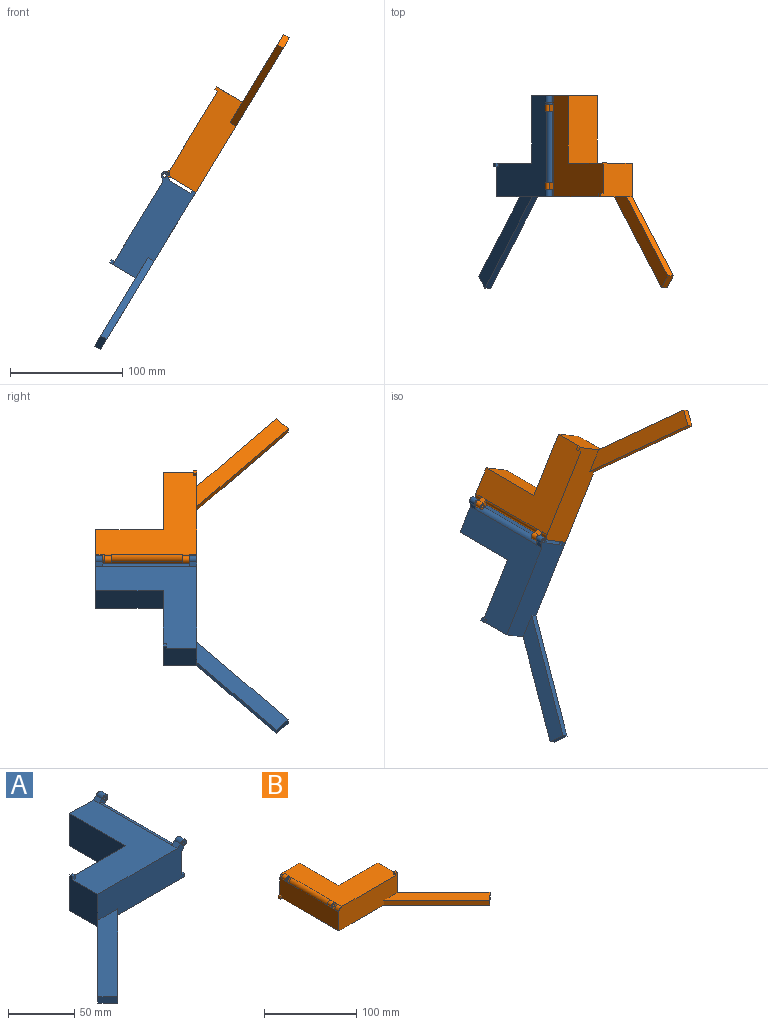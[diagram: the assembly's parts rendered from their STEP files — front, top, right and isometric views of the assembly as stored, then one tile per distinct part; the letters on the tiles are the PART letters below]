
ASSEMBLY  parts=2 mates=1
PART A: 29 faces, bbox 165.4x171.3x34.7 mm
  f0: plane 90x25.32mm, normal (1,0,0), area 2267mm2, adj f5,f9,f10,f13,f16,f17,f18,f21
  f1: plane 90x85.32mm, normal (0,0,1), area 4067mm2, adj f5,f6,f7,f8,f9,f13,f16,f19
  f2: plane 70.71x70.71mm, normal (-0.71,0.71,0), area 600mm2, adj f3,f8,f10,f22
  f3: plane 10.61x10.61mm, normal (-0.71,-0.71,0), area 90mm2, adj f2,f4,f10,f22
  f4: plane 81.32x81.32mm, normal (0.71,-0.71,0), area 690mm2, adj f3,f9,f10,f22
  f5: plane 34.68x34.68mm, normal (0,1,0), area 930.6mm2, adj f0,f1,f6,f10,f14,f15,f17,f20
  f6: plane 60x30mm, normal (-1,0,0), area 1800mm2, adj f1,f5,f7,f10
  f7: plane 60x32.96mm, normal (0,1,0), area 1809.2mm2, adj f1,f6,f8,f10,f24,f25
  f8: plane 32.96x30mm, normal (-1,0,0), area 909.2mm2, adj f1,f2,f7,f9,f10,f23,f25
  f9: plane 94.68x34.68mm, normal (0,-1,0), area 2612.5mm2, adj f0,f1,f4,f8,f10,f11,f12,f18
  f10: plane 171.32x163.67mm, normal (0,0,-1), area 6121.7mm2, adj f0,f2,f3,f4,f5,f6,f7,f8
  f11: cylinder r=3.12mm len=6.24mm, axis (0,-1,0), area 79.7mm2, adj f9,f13,f18,f19
  f12: cylinder r=1.56mm len=6.24mm, axis (0,-1,0), area 61.2mm2, adj f9,f13
  f13: plane 9.53x9.53mm, normal (0,1,0), area 35.3mm2, adj f0,f1,f11,f12,f18,f19,f21
  f14: cylinder r=3.12mm len=6.24mm, axis (0,1,0), area 79.7mm2, adj f5,f16,f17,f20
  f15: cylinder r=1.56mm len=6.24mm, axis (0,1,0), area 61.2mm2, adj f5,f16
  f16: plane 9.53x9.53mm, normal (0,-1,0), area 35.3mm2, adj f0,f1,f14,f15,f17,f20,f21
  f17: plane 6.24x3.43mm, normal (0.81,0,-0.59), area 26.5mm2, adj f0,f5,f14,f16
  f18: plane 6.24x3.43mm, normal (0.81,0,-0.59), area 26.5mm2, adj f0,f9,f11,f13
  f19: plane 6.24x3.43mm, normal (-0.59,0,0.81), area 26.5mm2, adj f1,f9,f11,f13
  f20: plane 6.24x3.43mm, normal (-0.59,0,0.81), area 26.5mm2, adj f1,f5,f14,f16
  f21: cylinder r=4.68mm len=77.52mm, axis (0,-1,0), area 569.9mm2, adj f0,f1,f13,f16
  f22: plane 91.92x81.32mm, normal (0,0,1), area 1612.5mm2, adj f2,f3,f4,f9
  f23: plane 3.12x2.96mm, normal (0,-1,0), area 9.2mm2, adj f1,f8,f24,f25
  f24: plane 3.12x2.96mm, normal (1,0,0), area 9.2mm2, adj f1,f7,f23,f25
  f25: plane 3.12x3.12mm, normal (0,0,1), area 9.7mm2, adj f7,f8,f23,f24
  f26: plane 3.12x2.96mm, normal (0,0,1), area 9.2mm2, adj f0,f9,f27,f28
  f27: plane 3.12x2.96mm, normal (0,1,0), area 9.2mm2, adj f0,f10,f26,f28
  f28: plane 3.12x3.12mm, normal (1,0,0), area 9.7mm2, adj f9,f10,f26,f27
PART B: 33 faces, bbox 165.4x171.3x34.7 mm
  f0: plane 90x25.32mm, normal (-1,0,0), area 2267mm2, adj f2,f9,f10,f13,f14,f17,f18,f19
  f1: plane 90x85.32mm, normal (0,0,1), area 4067mm2, adj f2,f3,f4,f5,f9,f13,f14,f17
  f2: plane 32.96x30mm, normal (0,1,0), area 904.5mm2, adj f0,f1,f3,f10,f25,f30,f32
  f3: plane 60x30mm, normal (1,0,0), area 1800mm2, adj f1,f2,f4,f10
  f4: plane 60x30mm, normal (0,1,0), area 1800mm2, adj f1,f3,f5,f10
  f5: plane 32.96x30mm, normal (1,0,0), area 909.2mm2, adj f1,f4,f6,f9,f10,f27,f29
  f6: plane 70.71x70.71mm, normal (0.71,0.71,0), area 600mm2, adj f5,f7,f10,f26
  f7: plane 10.61x10.61mm, normal (0.71,-0.71,0), area 90mm2, adj f6,f8,f10,f26
  f8: plane 81.32x81.32mm, normal (-0.71,-0.71,0), area 690mm2, adj f7,f9,f10,f26
  f9: plane 90x32.96mm, normal (0,-1,0), area 2577.3mm2, adj f0,f1,f5,f8,f10,f23,f26,f28
  f10: plane 171.32x163.67mm, normal (0,0,-1), area 6121.7mm2, adj f0,f2,f3,f4,f5,f6,f7,f8
  f11: cylinder r=1.56mm len=6.24mm, axis (0,1,0), area 61.2mm2, adj f13,f14
  f12: cylinder r=3.12mm len=6.24mm, axis (0,1,0), area 79.7mm2, adj f13,f14,f19,f21
  f13: plane 9.53x9.53mm, normal (0,-1,0), area 35.3mm2, adj f0,f1,f11,f12,f19,f21,f24
  f14: plane 9.53x9.53mm, normal (0,1,0), area 35.3mm2, adj f0,f1,f11,f12,f19,f21,f25
  f15: cylinder r=1.56mm len=6.24mm, axis (0,-1,0), area 61.2mm2, adj f17,f18
  f16: cylinder r=3.12mm len=6.24mm, axis (0,-1,0), area 79.7mm2, adj f17,f18,f20,f22
  f17: plane 9.53x9.53mm, normal (0,1,0), area 35.3mm2, adj f0,f1,f15,f16,f20,f22,f24
  f18: plane 9.53x9.53mm, normal (0,-1,0), area 35.3mm2, adj f0,f1,f15,f16,f20,f22,f23
  f19: plane 6.24x3.43mm, normal (-0.81,0,-0.59), area 26.5mm2, adj f0,f12,f13,f14
  f20: plane 6.24x3.43mm, normal (-0.81,0,-0.59), area 26.5mm2, adj f0,f16,f17,f18
  f21: plane 6.24x3.43mm, normal (0.59,0,0.81), area 26.5mm2, adj f1,f12,f13,f14
  f22: plane 6.24x3.43mm, normal (0.59,0,0.81), area 26.5mm2, adj f1,f16,f17,f18
  f23: cylinder r=4.68mm len=6.37mm, axis (0,-1,0), area 46.8mm2, adj f0,f1,f9,f18
  f24: cylinder r=4.68mm len=63.79mm, axis (0,-1,0), area 469mm2, adj f0,f1,f13,f17
  f25: cylinder r=4.68mm len=7.36mm, axis (0,-1,0), area 54.1mm2, adj f0,f1,f2,f14
  f26: plane 91.92x81.32mm, normal (0,0,1), area 1612.5mm2, adj f6,f7,f8,f9
  f27: plane 3.12x2.96mm, normal (0,1,0), area 9.2mm2, adj f1,f5,f28,f29
  f28: plane 3.12x2.96mm, normal (-1,0,0), area 9.2mm2, adj f1,f9,f27,f29
  f29: plane 3.12x3.12mm, normal (0,0,1), area 9.7mm2, adj f5,f9,f27,f28
  f30: plane 3.12x2.96mm, normal (0,0,1), area 9.2mm2, adj f0,f2,f31,f32
  f31: plane 3.12x2.96mm, normal (0,-1,0), area 9.2mm2, adj f0,f10,f30,f32
  f32: plane 3.12x3.12mm, normal (-1,0,0), area 9.7mm2, adj f2,f10,f30,f31
PLACE A rot(axis=(0,-1,0),58.8deg) t=(-90.45,40.75,-56.2)mm
PLACE B rot(axis=(0,-1,0),58.8deg) t=(-122.99,40.67,-109.88)mm
MATE cylindrical B.f11 <-> A.f14  axis (0,-1,0) through (-133.71,2.03,-66.68)mm
